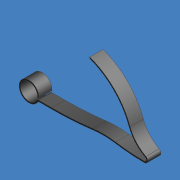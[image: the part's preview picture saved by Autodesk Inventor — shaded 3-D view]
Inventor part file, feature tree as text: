
AUTODESK INVENTOR PART (.ipt)
format: ipt  version: unknown  size: 209,408 bytes
history: native  units: mm (DEFAULTED — no unit token found)
features: extrude x1, sketch x1
ambient origin geometry x8: Origin, YZ Plane, XZ Plane, XY Plane, X Axis, Y Axis, Z Axis, Center Point
feature tree (2):
  extrude  "Extrusion2"  Depth=7.40714mm
  sketch  "Sketch1"  dims[d25=8.726646mm d26=7.40714mm d27=10.0mm d28=5.0mm d29=2.0mm d30=0.0mm d34=0.5mm d35=1.3mm d36=16.0mm]
